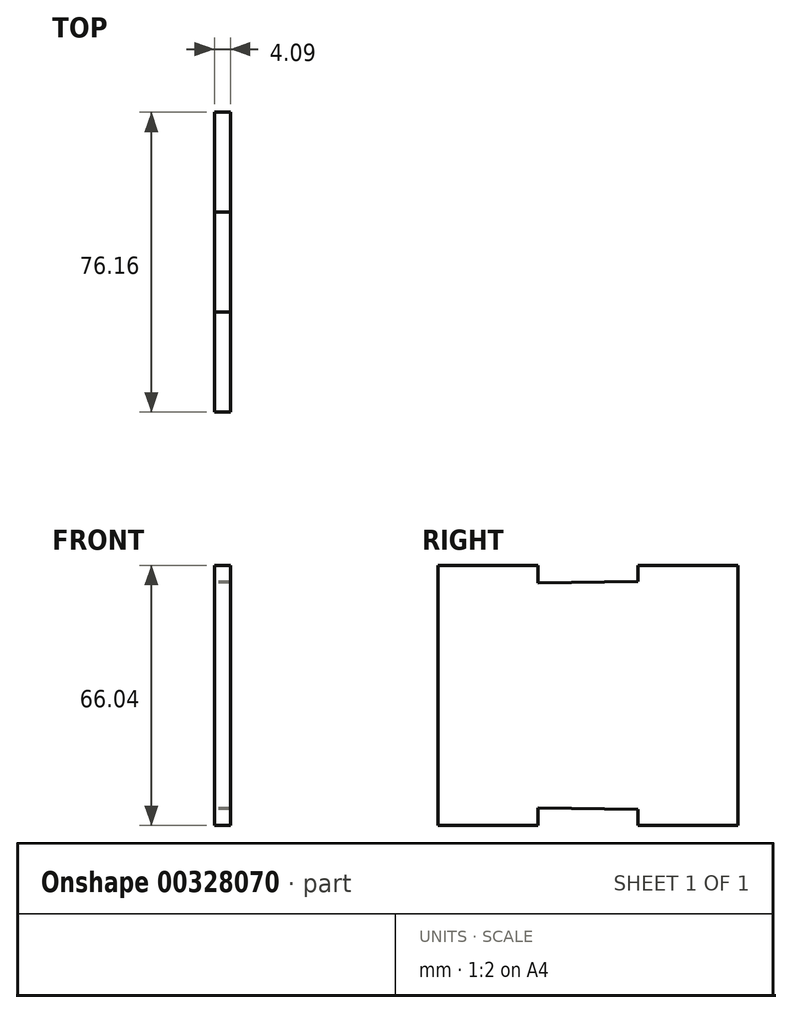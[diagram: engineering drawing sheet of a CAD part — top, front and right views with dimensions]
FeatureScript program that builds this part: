
annotation { "Feature Type Name" : "Feature", "Feature Type Description" : "" }
export const myFeature = defineFeature(function(context is Context, id is Id, definition is map)
    precondition{}
    {
        {
            var Q0;
            Q0=qCreatedBy(makeId("Right.planeOp"),FACE);
            var sketch = newSketch(context, id + "F0", { "sketchPlane" : qUnion([Q0])});
            skLineSegment(sketch, "E0.bottom", {"start": v(-38.17, -61.95) * mm, "end": v(-12.78, -61.95) * mm});
            skLineSegment(sketch, "E0.top", {"start": v(-38.17, 4.09) * mm, "end": v(-12.78, 4.09) * mm});
            skLineSegment(sketch, "E0.left", {"start": v(-38.17, -61.95) * mm, "end": v(-38.17, 4.09) * mm});
            skLineSegment(sketch, "E0.right", {"start": v(38, -61.95) * mm, "end": v(38, 4.09) * mm});
            skLineSegment(sketch, "E1.bottom", {"start": v(12.6, 0) * mm, "end": v(-12.8, -0.4) * mm});
            skLineSegment(sketch, "E1.left", {"start": v(12.6, 0) * mm, "end": v(12.61, 4.09) * mm});
            skLineSegment(sketch, "E1.right", {"start": v(-12.8, -0.4) * mm, "end": v(-12.78, 4.09) * mm});
            skPoint(sketch, "E1.middle", {"position": v(-0.09, 4.09) * mm});
            skPoint(sketch, "E1.top.end.orphan", {"position": v(-12.77, 8.18) * mm});
            skLineSegment(sketch, "E2.trimOffspring", {"start": v(12.61, 4.09) * mm, "end": v(38, 4.09) * mm});
            skPoint(sketch, "E3.orphan", {"position": v(12.63, 8.58) * mm});
            skLineSegment(sketch, "E4", {"start": v(-38.17, -28.93) * mm, "end": v(38, -28.93) * mm, "construction": true});
            skLineSegment(sketch, "E5.MirrorCS", {"start": v(12.6, -57.86) * mm, "end": v(-12.8, -57.46) * mm});
            skLineSegment(sketch, "E6.MirrorCS", {"start": v(-12.8, -57.46) * mm, "end": v(-12.78, -61.95) * mm});
            skLineSegment(sketch, "E7.MirrorCS", {"start": v(12.6, -57.86) * mm, "end": v(12.61, -61.95) * mm});
            skLineSegment(sketch, "E8.trimOffspring", {"start": v(12.61, -61.95) * mm, "end": v(38, -61.95) * mm});
            skLineSegment(sketch, "E9", {"start": v(0, 0) * mm, "end": v(0, -57.66) * mm, "construction": true});
            skSolve(sketch);
        }
        {
            var Q0;
            Q0 = qSketchRegion(id + "F0", true);
            extrude(context, id + "F1", {"entities" : qUnion([Q0]), "depth" : 4.1 * mm});
        }
    });
